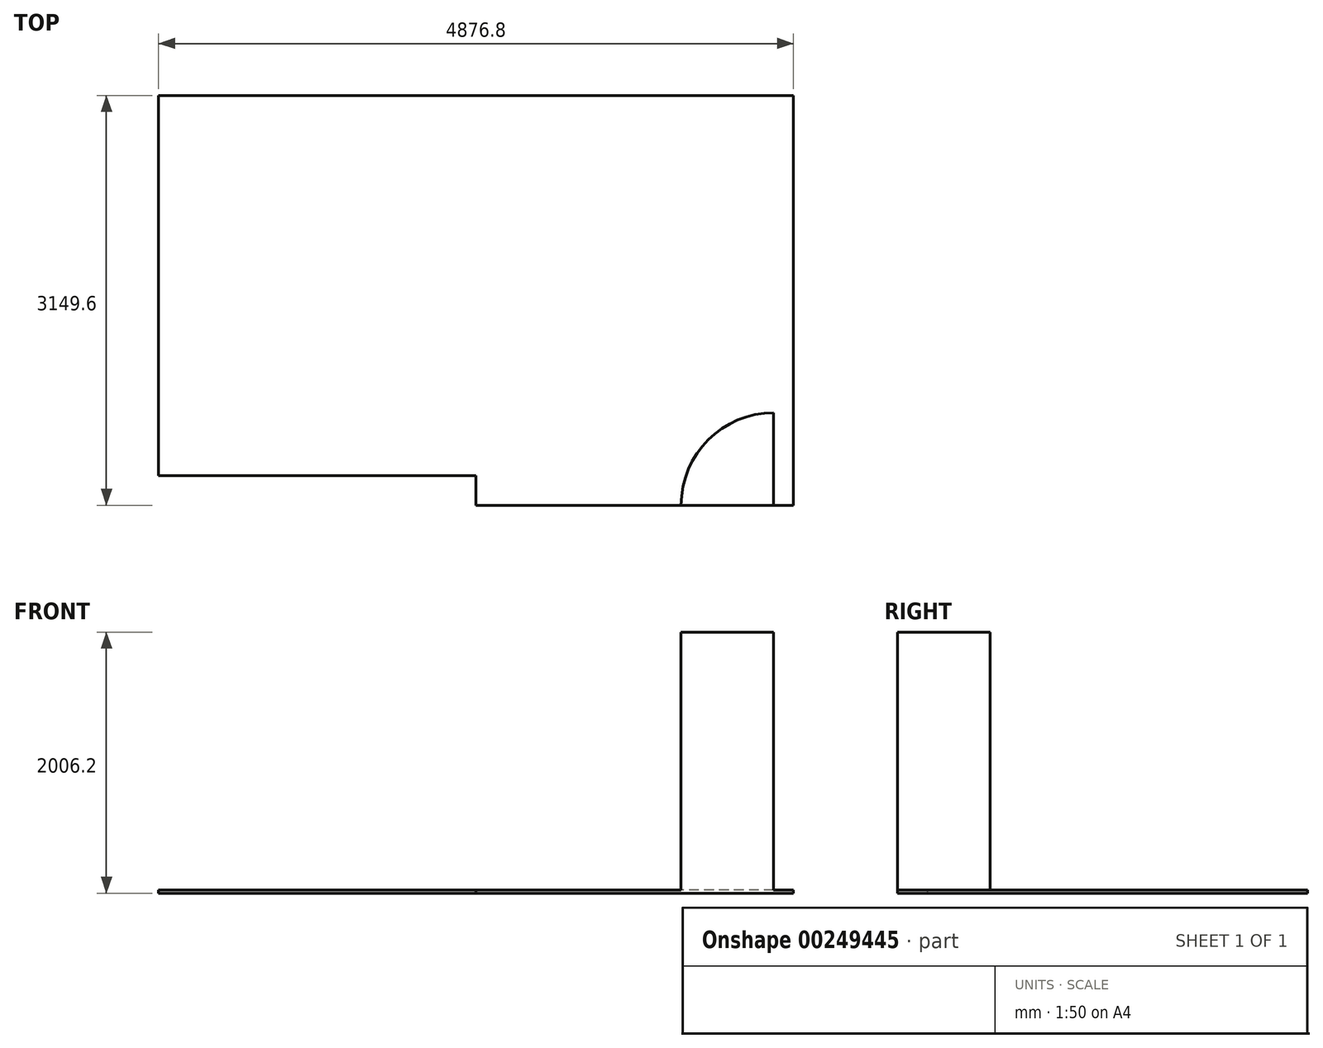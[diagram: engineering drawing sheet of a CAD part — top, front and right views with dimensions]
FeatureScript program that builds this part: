
annotation { "Feature Type Name" : "Feature", "Feature Type Description" : "" }
export const myFeature = defineFeature(function(context is Context, id is Id, definition is map)
    precondition{}
    {
        {
            var Q0;
            Q0=qCreatedBy(makeId("Top.planeOp"),FACE);
            var sketch = newSketch(context, id + "F0", { "sketchPlane" : qUnion([Q0])});
            skLineSegment(sketch, "E0", {"start": v(0, 0) * mm, "end": v(4876.8, 0) * mm});
            skLineSegment(sketch, "E1", {"start": v(4876.8, 0) * mm, "end": v(4876.8, -3149.6) * mm});
            skLineSegment(sketch, "E2", {"start": v(4876.8, -3149.6) * mm, "end": v(2438.4, -3149.6) * mm});
            skLineSegment(sketch, "E3", {"start": v(2438.4, -3149.6) * mm, "end": v(2438.4, -2921) * mm});
            skLineSegment(sketch, "E4", {"start": v(2438.4, -2921) * mm, "end": v(0, -2921) * mm});
            skLineSegment(sketch, "E5", {"start": v(0, -2921) * mm, "end": v(0, 0) * mm});
            skSolve(sketch);
        }
        {
            var Q0;
            Q0 = qSketchRegion(id + "F0", true);
            extrude(context, id + "F1", {"entities" : qUnion([Q0]), "depth" : 25 * mm});
        }
        {
            var Q0;
            Q0=makeQuery(id+"F1.opExtrude","CAP_FACE",FACE,{"disambiguationData":[OSD([sQuery(id+"F0.wireOp",EDGE,"E0"),sQuery(id+"F0.wireOp",EDGE,"E1"),sQuery(id+"F0.wireOp",EDGE,"E2"),sQuery(id+"F0.wireOp",EDGE,"E3"),sQuery(id+"F0.wireOp",EDGE,"E4"),sQuery(id+"F0.wireOp",EDGE,"E5")])],"isStart":false});
            var sketch = newSketch(context, id + "F2", { "sketchPlane" : qUnion([Q0])});
            skLineSegment(sketch, "E6", {"start": v(4724.4, -3149.6) * mm, "end": v(4724.4, -2438.4) * mm});
            skArc(sketch, "E7", {"start": v(4724.4, -2438.4) * mm, "mid": v(4221.5, -2646.7) * mm, "end": v(4013.2, -3149.6) * mm});
            skLineSegment(sketch, "E8", {"start": v(4724.4, -3149.6) * mm, "end": v(4013.2, -3149.6) * mm});
            skSolve(sketch);
        }
        {
            var Q0;
            Q0 = qSketchRegion(id + "F2", true);
            extrude(context, id + "F3", {"entities" : qUnion([Q0]), "operationType" : NewBodyOperationType.ADD, "depth" : 1981.2 * mm});
        }
    });
